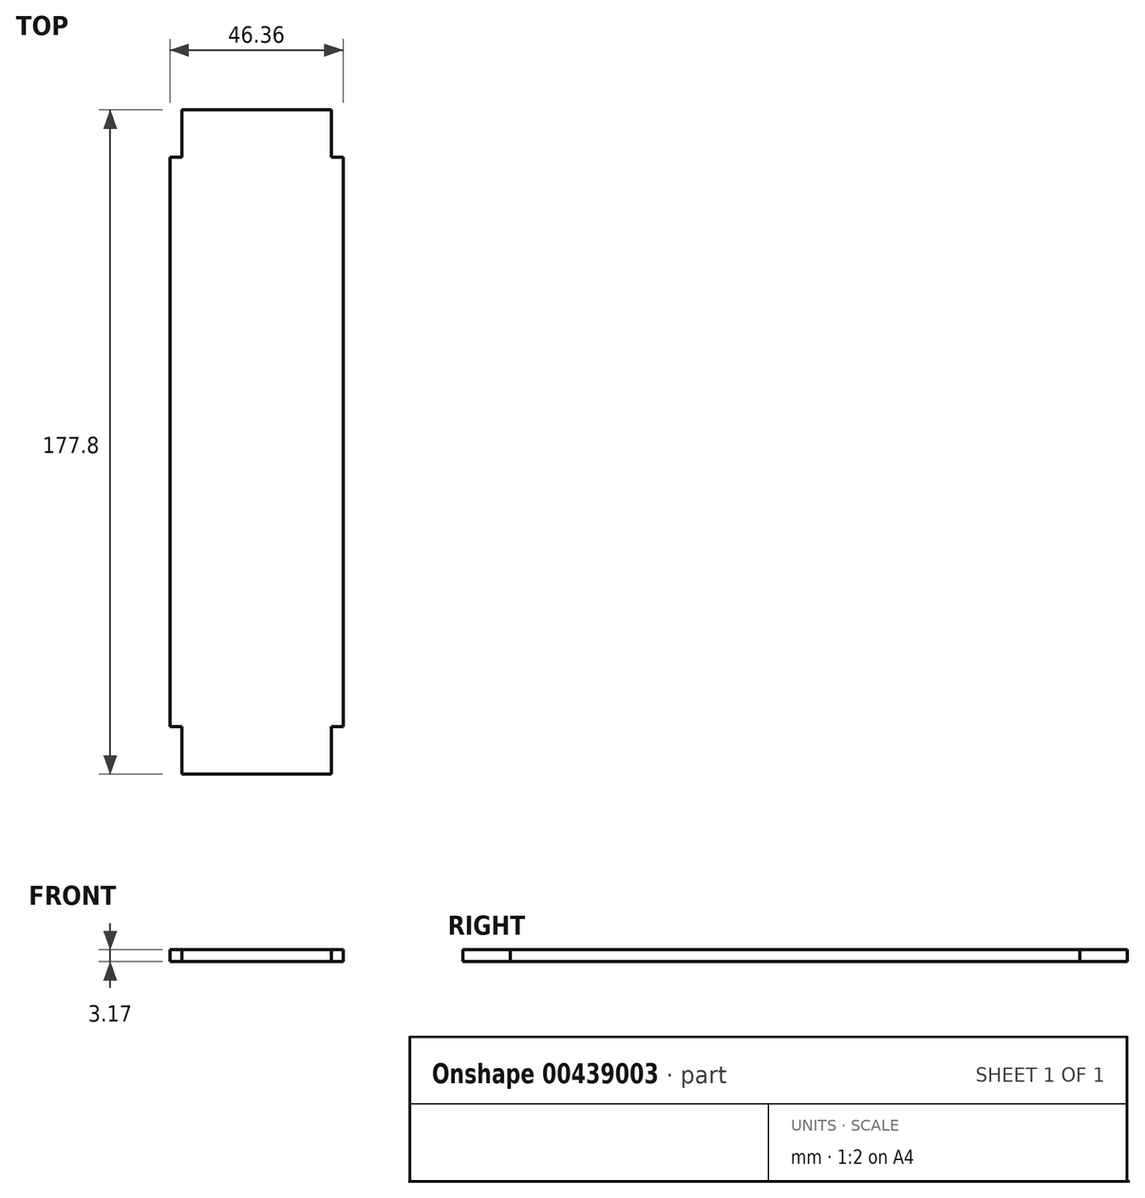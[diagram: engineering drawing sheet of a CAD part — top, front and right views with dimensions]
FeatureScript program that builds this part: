
annotation { "Feature Type Name" : "Feature", "Feature Type Description" : "" }
export const myFeature = defineFeature(function(context is Context, id is Id, definition is map)
    precondition{}
    {
        {
            var Q0;
            Q0=qCreatedBy(makeId("Top.planeOp"),FACE);
            var sketch = newSketch(context, id + "F0", { "sketchPlane" : qUnion([Q0])});
            skLineSegment(sketch, "E0.bottom", {"start": v(20, -88.9) * mm, "end": v(-20, -88.9) * mm});
            skLineSegment(sketch, "E0.top", {"start": v(20, 88.9) * mm, "end": v(-20, 88.9) * mm});
            skLineSegment(sketch, "E0.left", {"start": v(20, -88.9) * mm, "end": v(20, 88.9) * mm});
            skLineSegment(sketch, "E0.right", {"start": v(-20, -88.9) * mm, "end": v(-20, 88.9) * mm});
            skPoint(sketch, "E0.middle", {"position": v(0, 0) * mm});
            skSolve(sketch);
        }
        {
            var Q0;
            Q0=makeQuery(id+"F0.imprint","IMPRINT",FACE,{"disambiguationData":[TD([[makeQuery(id+"F0.imprint","IMPRINT",EDGE,{"derivedFrom":sQuery(id+"F0.wireOp",EDGE,"E0.bottom")}),-1.0]])]});
            extrude(context, id + "F1", {"entities" : qUnion([Q0]), "depth" : 3.17 * mm, "offsetDistance" : 25.4 * mm});
        }
        {
            var Q0;
            Q0=makeQuery(id+"F1.opExtrude","SWEPT_FACE",FACE,{"disambiguationData":[OSD([sQuery(id+"F0.wireOp",EDGE,"E0.right")])]});
            var sketch = newSketch(context, id + "F2", { "sketchPlane" : qUnion([Q0])});
            skLineSegment(sketch, "E1", {"start": v(0, 0) * mm, "end": v(0, 3.18) * mm, "construction": true});
            skPoint(sketch, "E2", {"position": v(0, 1.59) * mm});
            skLineSegment(sketch, "E3.bottom", {"start": v(76.2, 0) * mm, "end": v(-76.2, 0) * mm});
            skLineSegment(sketch, "E3.top", {"start": v(76.2, 3.18) * mm, "end": v(-76.2, 3.17) * mm});
            skLineSegment(sketch, "E3.left", {"start": v(76.2, 0) * mm, "end": v(76.2, 3.18) * mm});
            skLineSegment(sketch, "E3.right", {"start": v(-76.2, 0) * mm, "end": v(-76.2, 3.17) * mm});
            skSolve(sketch);
        }
        {
            var Q0;
            Q0=makeQuery(id+"F2.imprint","IMPRINT",FACE,{"disambiguationData":[TD([[makeQuery(id+"F2.imprint","IMPRINT",EDGE,{"derivedFrom":sQuery(id+"F2.wireOp",EDGE,"E3.bottom")}),-1.0]])]});
            extrude(context, id + "F3", {"entities" : qUnion([Q0]), "operationType" : NewBodyOperationType.ADD, "depth" : 3.17 * mm, "offsetDistance" : 25.4 * mm});
        }
        {
            var Q0;
            Q0=makeQuery(id+"F1.opExtrude","SWEPT_FACE",FACE,{"disambiguationData":[OSD([sQuery(id+"F0.wireOp",EDGE,"E0.left")])]});
            var sketch = newSketch(context, id + "F4", { "sketchPlane" : qUnion([Q0])});
            skLineSegment(sketch, "E4", {"start": v(0, 0) * mm, "end": v(0, 3.18) * mm, "construction": true});
            skPoint(sketch, "E5", {"position": v(0, 1.59) * mm});
            skLineSegment(sketch, "E6.bottom", {"start": v(76.2, 0) * mm, "end": v(-76.2, 0) * mm});
            skLineSegment(sketch, "E6.top", {"start": v(76.2, 3.18) * mm, "end": v(-76.2, 3.17) * mm});
            skLineSegment(sketch, "E6.left", {"start": v(76.2, 0) * mm, "end": v(76.2, 3.18) * mm});
            skLineSegment(sketch, "E6.right", {"start": v(-76.2, 0) * mm, "end": v(-76.2, 3.17) * mm});
            skSolve(sketch);
        }
        {
            var Q0;
            Q0=makeQuery(id+"F4.imprint","IMPRINT",FACE,{"disambiguationData":[TD([[makeQuery(id+"F4.imprint","IMPRINT",EDGE,{"derivedFrom":sQuery(id+"F4.wireOp",EDGE,"E6.bottom")}),1.0]])]});
            extrude(context, id + "F5", {"entities" : qUnion([Q0]), "operationType" : NewBodyOperationType.ADD, "depth" : 3.17 * mm, "offsetDistance" : 25.4 * mm});
        }
    });
